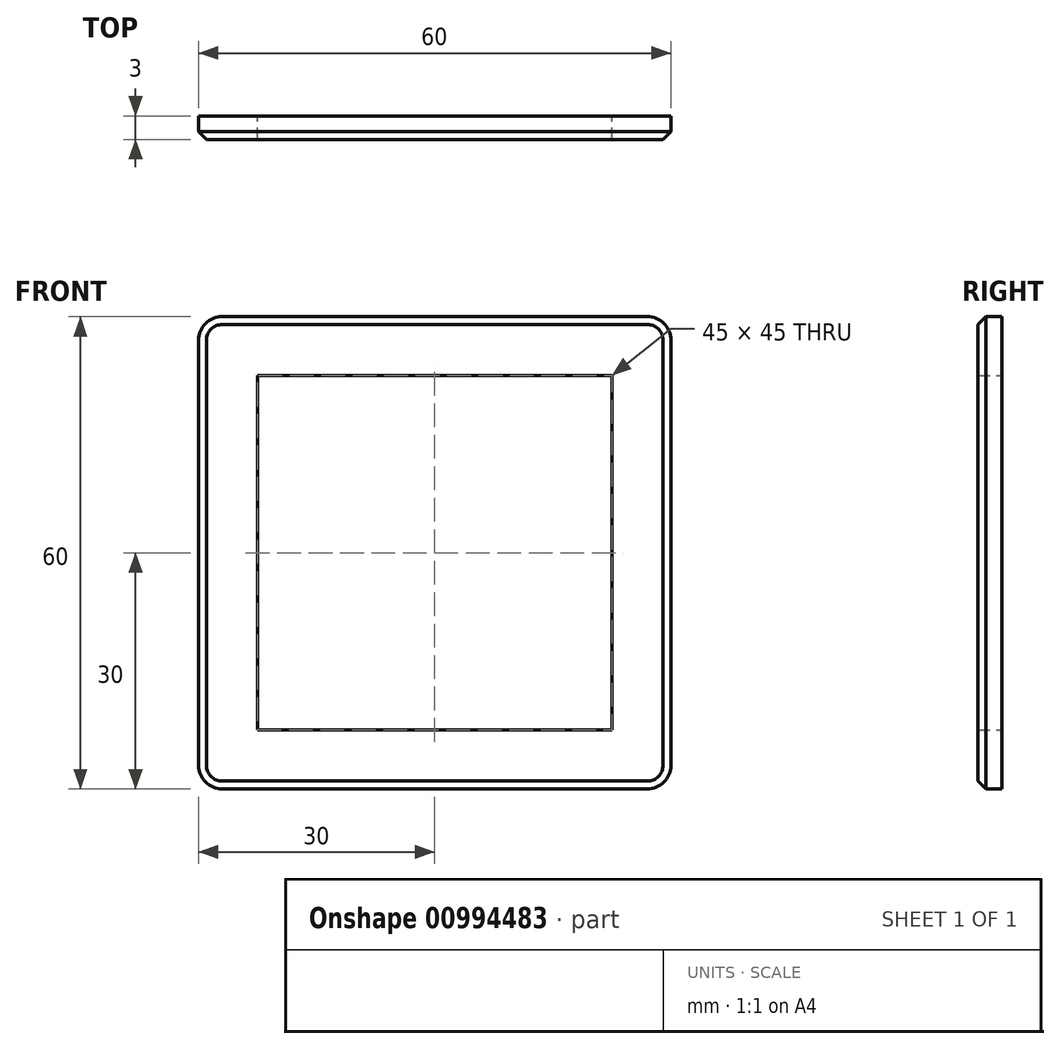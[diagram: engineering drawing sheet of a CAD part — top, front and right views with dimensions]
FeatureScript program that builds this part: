
annotation { "Feature Type Name" : "Feature", "Feature Type Description" : "" }
export const myFeature = defineFeature(function(context is Context, id is Id, definition is map)
    precondition{}
    {
        {
            var Q0;
            Q0=qCreatedBy(makeId("Front.planeOp"),FACE);
            var sketch = newSketch(context, id + "F0", { "sketchPlane" : qUnion([Q0])});
            skLineSegment(sketch, "E0.bottom", {"start": v(-27, 30) * mm, "end": v(27, 30) * mm});
            skLineSegment(sketch, "E0.top", {"start": v(-27, -30) * mm, "end": v(27, -30) * mm});
            skLineSegment(sketch, "E0.left", {"start": v(-30, 27) * mm, "end": v(-30, -27) * mm});
            skLineSegment(sketch, "E0.right", {"start": v(30, 27) * mm, "end": v(30, -27) * mm});
            skLineSegment(sketch, "E1", {"start": v(0, 30) * mm, "end": v(0, 22.5) * mm, "construction": true});
            skLineSegment(sketch, "E2", {"start": v(30, 0) * mm, "end": v(22.5, 0) * mm, "construction": true});
            skLineSegment(sketch, "E3", {"start": v(0, 0) * mm, "end": v(-22.5, 0) * mm, "construction": true});
            skLineSegment(sketch, "E4", {"start": v(0, 0) * mm, "end": v(0, -22.5) * mm, "construction": true});
            skLineSegment(sketch, "E5.left", {"start": v(-22.5, 22.5) * mm, "end": v(-22.5, -22.5) * mm});
            skLineSegment(sketch, "E5.right", {"start": v(22.5, 22.5) * mm, "end": v(22.5, -22.5) * mm});
            skLineSegment(sketch, "E6", {"start": v(22.5, 0) * mm, "end": v(0, 0) * mm, "construction": true});
            skLineSegment(sketch, "E7", {"start": v(-22.5, 0) * mm, "end": v(-30, 0) * mm, "construction": true});
            skLineSegment(sketch, "E8", {"start": v(0, -22.5) * mm, "end": v(0, -30) * mm, "construction": true});
            skLineSegment(sketch, "E9", {"start": v(-22.5, -22.5) * mm, "end": v(22.5, -22.5) * mm});
            skPoint(sketch, "E10", {"position": v(0, -22.5) * mm});
            skLineSegment(sketch, "E11", {"start": v(-22.5, 22.5) * mm, "end": v(22.5, 22.5) * mm});
            skLineSegment(sketch, "E12", {"start": v(0, 22.5) * mm, "end": v(0, 0) * mm, "construction": true});
            skPoint(sketch, "E13.visualSharp", {"position": v(-30, 30) * mm});
            skArc(sketch, "E13.filletArc", {"start": v(-27, 30) * mm, "mid": v(-29.12, 29.12) * mm, "end": v(-30, 27) * mm});
            skPoint(sketch, "E14.visualSharp", {"position": v(30, 30) * mm});
            skArc(sketch, "E14.filletArc", {"start": v(30, 27) * mm, "mid": v(29.12, 29.12) * mm, "end": v(27, 30) * mm});
            skPoint(sketch, "E15.visualSharp", {"position": v(30, -30) * mm});
            skArc(sketch, "E15.filletArc", {"start": v(27, -30) * mm, "mid": v(29.12, -29.12) * mm, "end": v(30, -27) * mm});
            skPoint(sketch, "E16.visualSharp", {"position": v(-30, -30) * mm});
            skArc(sketch, "E16.filletArc", {"start": v(-30, -27) * mm, "mid": v(-29.12, -29.12) * mm, "end": v(-27, -30) * mm});
            skSolve(sketch);
        }
        {
            var Q0;
            Q0=makeQuery(id+"F0.imprint","IMPRINT",FACE,{"disambiguationData":[TD([[makeQuery(id+"F0.imprint","IMPRINT",EDGE,{"derivedFrom":sQuery(id+"F0.wireOp",EDGE,"E0.bottom")}),-1.0]])]});
            extrude(context, id + "F1", {"entities" : qUnion([Q0]), "depth" : 3 * mm, "offsetDistance" : 25 * mm});
        }
        {
            var Q0;
            Q0=makeQuery(id+"F1.opExtrude","CAP_EDGE",EDGE,{"disambiguationData":[OSD([sQuery(id+"F0.wireOp",EDGE,"E0.left")])],"isStart":false});
            var Q1;
            Q1=makeQuery(id+"F1.opExtrude","CAP_EDGE",EDGE,{"disambiguationData":[OSD([sQuery(id+"F0.wireOp",EDGE,"E0.bottom")])],"isStart":false});
            var Q2;
            Q2=makeQuery(id+"F1.opExtrude","CAP_EDGE",EDGE,{"disambiguationData":[OSD([sQuery(id+"F0.wireOp",EDGE,"E0.right")])],"isStart":false});
            var Q3;
            Q3=makeQuery(id+"F1.opExtrude","CAP_EDGE",EDGE,{"disambiguationData":[OSD([sQuery(id+"F0.wireOp",EDGE,"E0.top")])],"isStart":false});
            chamfer(context, id + "F2", {"entities" : qUnion([Q0, Q1, Q2, Q3]), "width" : 1 * mm, "tangentPropagation" : true});
        }
    });
